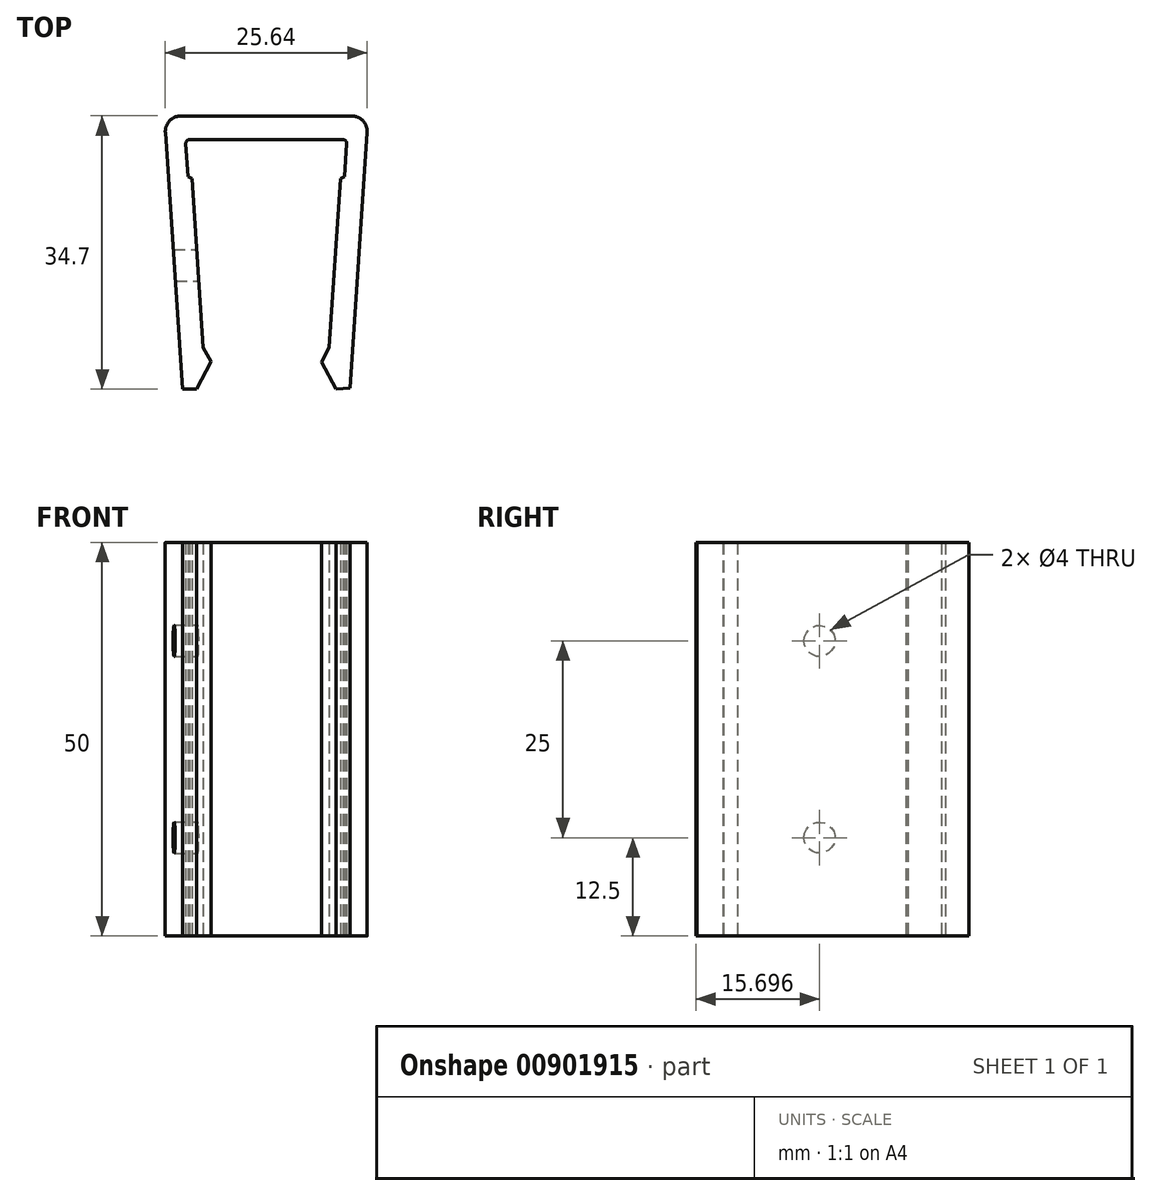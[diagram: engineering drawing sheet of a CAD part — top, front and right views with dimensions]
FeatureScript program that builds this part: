
annotation { "Feature Type Name" : "Feature", "Feature Type Description" : "" }
export const myFeature = defineFeature(function(context is Context, id is Id, definition is map)
    precondition{}
    {
        {
            var Q0;
            Q0=qCreatedBy(makeId("Top.planeOp"),FACE);
            var sketch = newSketch(context, id + "F0", { "sketchPlane" : qUnion([Q0])});
            skLineSegment(sketch, "E0", {"start": v(-9.75, 18.57) * mm, "end": v(9.75, 18.57) * mm});
            skLineSegment(sketch, "E1", {"start": v(9.75, 18.57) * mm, "end": v(9.75, 18.57) * mm});
            skLineSegment(sketch, "E2", {"start": v(-8, -7.88) * mm, "end": v(-9.42, 13.57) * mm});
            skLineSegment(sketch, "E3", {"start": v(-10.66, -13.13) * mm, "end": v(-12.81, 19.43) * mm});
            skLineSegment(sketch, "E4", {"start": v(-10.82, 21.57) * mm, "end": v(10.82, 21.57) * mm});
            skLineSegment(sketch, "E5", {"start": v(12.81, 19.43) * mm, "end": v(10.67, -13.02) * mm});
            skLineSegment(sketch, "E6", {"start": v(-8, -7.88) * mm, "end": v(-8, -9.63) * mm, "construction": true});
            skLineSegment(sketch, "E7", {"start": v(-8, -9.63) * mm, "end": v(-7, -9.63) * mm, "construction": true});
            skLineSegment(sketch, "E8", {"start": v(-8, -7.88) * mm, "end": v(-7, -9.63) * mm});
            skLineSegment(sketch, "E9", {"start": v(-7, -9.63) * mm, "end": v(-8.87, -13.13) * mm});
            skLineSegment(sketch, "E10", {"start": v(-8.87, -13.13) * mm, "end": v(-10.66, -13.13) * mm});
            skPoint(sketch, "E11.orphan", {"position": v(-10.37, -17.55) * mm});
            skLineSegment(sketch, "E12", {"start": v(8, -7.88) * mm, "end": v(8, -9.7) * mm, "construction": true});
            skLineSegment(sketch, "E13", {"start": v(8, -9.7) * mm, "end": v(7, -9.7) * mm, "construction": true});
            skLineSegment(sketch, "E14", {"start": v(8, -7.88) * mm, "end": v(7, -9.7) * mm});
            skLineSegment(sketch, "E15", {"start": v(7, -9.7) * mm, "end": v(8.88, -13.13) * mm});
            skLineSegment(sketch, "E16", {"start": v(8.88, -13.13) * mm, "end": v(10.67, -13.02) * mm});
            skPoint(sketch, "E17.orphan", {"position": v(10.37, -17.55) * mm});
            skPoint(sketch, "E18", {"position": v(9.42, 13.57) * mm});
            skPoint(sketch, "E19", {"position": v(-9.42, 13.57) * mm});
            skLineSegment(sketch, "E20", {"start": v(-10.22, 18.07) * mm, "end": v(-9.94, 13.82) * mm});
            skLineSegment(sketch, "E21", {"start": v(10.22, 18.03) * mm, "end": v(9.94, 13.82) * mm});
            skPoint(sketch, "E22", {"position": v(-9.72, 18.07) * mm});
            skArc(sketch, "E23", {"start": v(-9.75, 18.57) * mm, "mid": v(-10.08, 18.4) * mm, "end": v(-10.22, 18.07) * mm});
            skPoint(sketch, "E24", {"position": v(9.72, 18.07) * mm});
            skArc(sketch, "E25", {"start": v(10.22, 18.03) * mm, "mid": v(10.1, 18.4) * mm, "end": v(9.75, 18.57) * mm});
            skLineSegment(sketch, "E26", {"start": v(9.42, 13.57) * mm, "end": v(9.94, 13.82) * mm});
            skLineSegment(sketch, "E27", {"start": v(-9.42, 13.57) * mm, "end": v(-9.94, 13.82) * mm});
            skLineSegment(sketch, "E28.trimOffspring", {"start": v(9.42, 13.57) * mm, "end": v(8, -7.88) * mm});
            skPoint(sketch, "E29.visualSharp", {"position": v(-12.96, 21.57) * mm});
            skArc(sketch, "E29.filletArc", {"start": v(-10.82, 21.57) * mm, "mid": v(-12.28, 20.93) * mm, "end": v(-12.81, 19.43) * mm});
            skPoint(sketch, "E30.visualSharp", {"position": v(12.96, 21.57) * mm});
            skArc(sketch, "E30.filletArc", {"start": v(12.81, 19.43) * mm, "mid": v(12.28, 20.93) * mm, "end": v(10.82, 21.57) * mm});
            skSolve(sketch);
        }
        {
            var Q0;
            Q0=makeQuery(id+"F0.imprint","IMPRINT",FACE,{"disambiguationData":[TD([[makeQuery(id+"F0.imprint","IMPRINT",EDGE,{"derivedFrom":sQuery(id+"F0.wireOp",EDGE,"E0")}),1.0]])]});
            extrude(context, id + "F1", {"entities" : qUnion([Q0]), "depth" : 50 * mm, "offsetDistance" : 25 * mm});
        }
        {
            var Q0;
            Q0=qCreatedBy(makeId("Right.planeOp"),FACE);
            var sketch = newSketch(context, id + "F2", { "sketchPlane" : qUnion([Q0])});
            skCircle(sketch, "E31", {"center": v(2.57, 12.5) * mm, "radius": 2 * mm});
            skCircle(sketch, "E32", {"center": v(2.57, 37.5) * mm, "radius": 2 * mm});
            skSolve(sketch);
        }
        {
            var Q0;
            Q0=makeQuery(id+"F2.imprint","IMPRINT",FACE,{"disambiguationData":[TD([[makeQuery(id+"F2.imprint","IMPRINT",EDGE,{"derivedFrom":sQuery(id+"F2.wireOp",EDGE,"E31")}),1.0]])]});
            var Q1;
            Q1=makeQuery(id+"F2.imprint","IMPRINT",FACE,{"disambiguationData":[TD([[makeQuery(id+"F2.imprint","IMPRINT",EDGE,{"derivedFrom":sQuery(id+"F2.wireOp",EDGE,"E32")}),1.0]])]});
            extrude(context, id + "F3", {"entities" : qUnion([Q0, Q1]), "operationType" : NewBodyOperationType.REMOVE, "oppositeDirection" : true, "depth" : 25 * mm, "offsetDistance" : 25 * mm});
        }
    });
